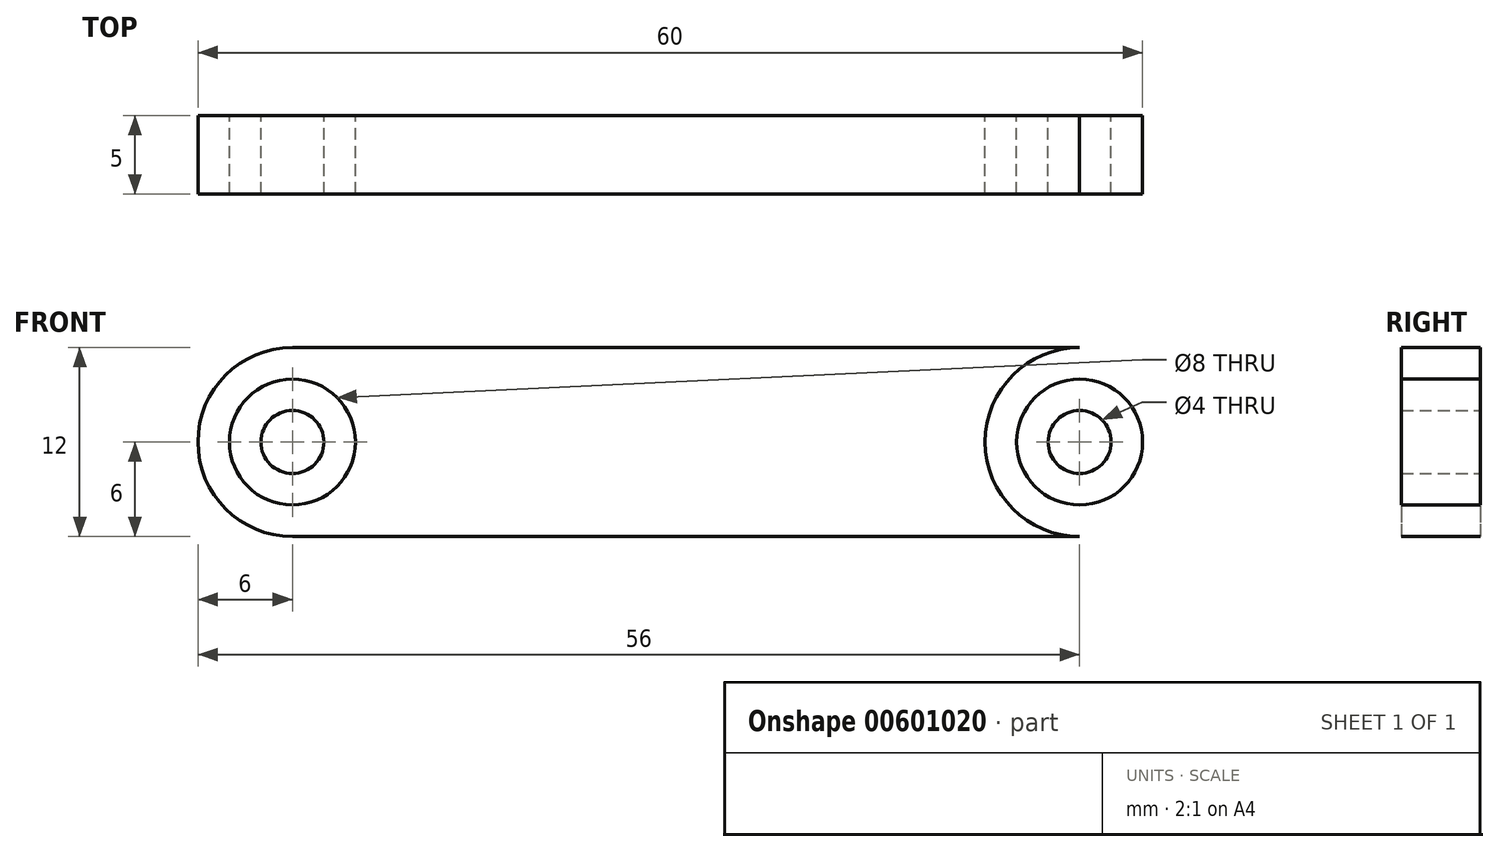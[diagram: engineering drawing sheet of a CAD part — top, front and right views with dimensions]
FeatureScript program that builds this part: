
annotation { "Feature Type Name" : "Feature", "Feature Type Description" : "" }
export const myFeature = defineFeature(function(context is Context, id is Id, definition is map)
    precondition{}
    {
        {
            var Q0;
            Q0=qCreatedBy(makeId("Front.planeOp"),FACE);
            var sketch = newSketch(context, id + "F0", { "sketchPlane" : qUnion([Q0])});
            skCircle(sketch, "E0", {"center": v(-25, 0) * mm, "radius": 6 * mm});
            skCircle(sketch, "E1", {"center": v(-25, 0) * mm, "radius": 4 * mm});
            skCircle(sketch, "E2", {"center": v(-25, 0) * mm, "radius": 2 * mm});
            skLineSegment(sketch, "E3", {"start": v(-25, 6) * mm, "end": v(0, 6) * mm});
            skLineSegment(sketch, "E4", {"start": v(-25, -6) * mm, "end": v(0, -6) * mm});
            skCircle(sketch, "E5.MirrorC", {"center": v(25, 0) * mm, "radius": 2 * mm});
            skCircle(sketch, "E6.MirrorC", {"center": v(25, 0) * mm, "radius": 4 * mm});
            skLineSegment(sketch, "E7.MirrorCS", {"start": v(25, -6) * mm, "end": v(0, -6) * mm});
            skLineSegment(sketch, "E8.MirrorCS", {"start": v(25, 6) * mm, "end": v(0, 6) * mm});
            skCircle(sketch, "E9.MirrorC", {"center": v(25, 0) * mm, "radius": 6 * mm});
            skSolve(sketch);
        }
        {
            var Q0;
            Q0=makeQuery(id+"F0.imprint","IMPRINT",FACE,{"disambiguationData":[TD([[makeQuery(id+"F0.imprint","IMPRINT",EDGE,{"derivedFrom":sQuery(id+"F0.wireOp",EDGE,"E2")}),1.0]])]});
            var Q1;
            Q1=makeQuery(id+"F0.imprint","IMPRINT",FACE,{"disambiguationData":[TD([[makeQuery(id+"F0.imprint","IMPRINT",EDGE,{"derivedFrom":sQuery(id+"F0.wireOp",EDGE,"E1")}),-1.0]])]});
            var Q2;
            {var subQ2=sQuery(id+"F0.wireOp",EDGE,"E3");Q2=makeQuery(id+"F0.imprint","IMPRINT",FACE,{"disambiguationData":[TD([[makeQuery(id+"F0.imprint","IMPRINT",EDGE,{"derivedFrom":subQ2}),-1.0]])]});}
            var Q3;
            Q3=makeQuery(id+"F0.imprint","IMPRINT",FACE,{"disambiguationData":[TD([[makeQuery(id+"F0.imprint","IMPRINT",EDGE,{"derivedFrom":sQuery(id+"F0.wireOp",EDGE,"E6.MirrorC")}),1.0]])]});
            var Q4;
            Q4=makeQuery(id+"F0.imprint","IMPRINT",FACE,{"disambiguationData":[TD([[makeQuery(id+"F0.imprint","IMPRINT",EDGE,{"derivedFrom":sQuery(id+"F0.wireOp",EDGE,"E5.MirrorC")}),-1.0]])]});
            extrude(context, id + "F1", {"entities" : qUnion([Q0, Q1, Q2, Q3, Q4]), "depth" : 5 * mm, "offsetDistance" : 25 * mm});
        }
    });
